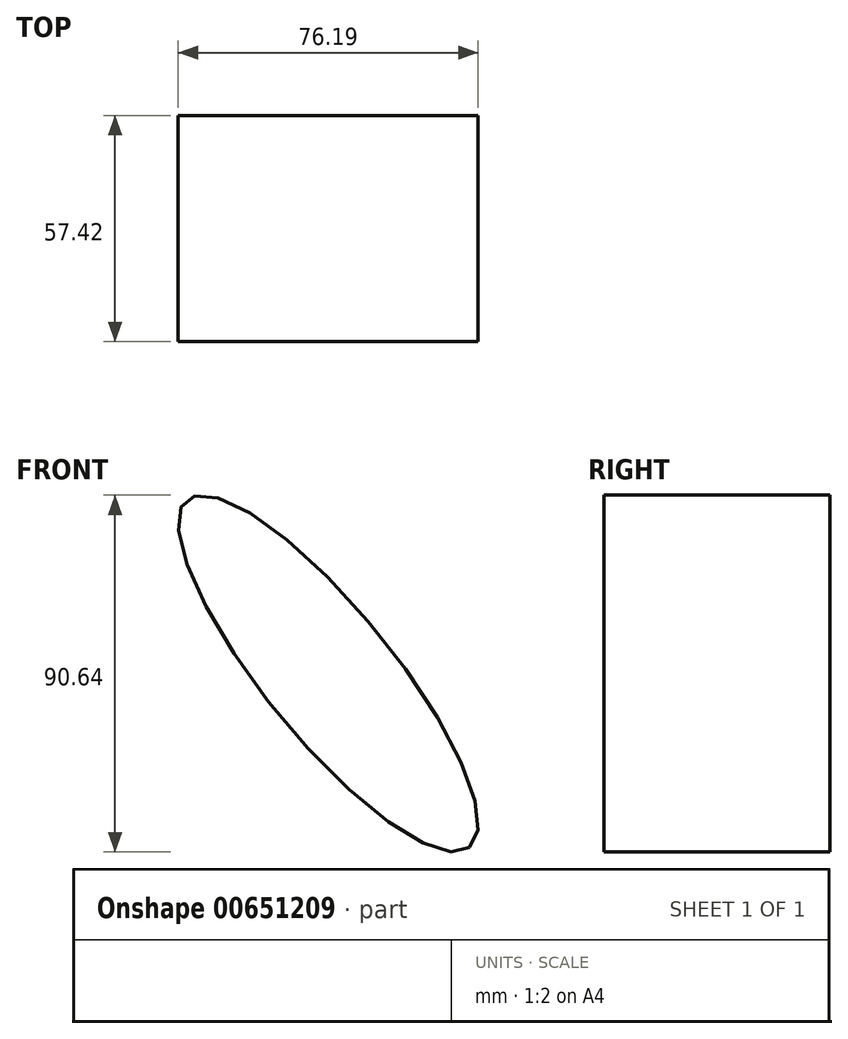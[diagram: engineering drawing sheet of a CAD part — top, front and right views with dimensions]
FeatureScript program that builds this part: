
annotation { "Feature Type Name" : "Feature", "Feature Type Description" : "" }
export const myFeature = defineFeature(function(context is Context, id is Id, definition is map)
    precondition{}
    {
        {
            var Q0;
            Q0=qCreatedBy(makeId("Front.planeOp"),FACE);
            var sketch = newSketch(context, id + "F0", { "sketchPlane" : qUnion([Q0])});
            skEllipse(sketch, "E0", {"center": v(56.7, 0) * mm, "majorRadius": 16.3 * mm, "minorRadius": 56.92 * mm, "majorAxis": v(-0.78, -0.63)});
            skSolve(sketch);
        }
        {
            var Q0;
            Q0 = qSketchRegion(id + "F0", true);
            extrude(context, id + "F1", {"entities" : qUnion([Q0]), "depth" : 57.42 * mm, "offsetDistance" : 25.4 * mm});
        }
    });
